# Revit family: equip-sink-clsrm-elkay-s-pacemaker-psdkrc2517-vrc
name_source: partatom
category: Plumbing Fixtures
units: mm (PartAtom-declared; Revit-internal decimal feet)

## family parameters
Always vertical = Yes
Cut with Voids When Loaded = No
OmniClass Number = 23.45.05.14.14.27
OmniClass Title = Service Sinks
Part Type = Normal
Room Calculation Point = No
Round Connector Dimension = Use Radius
Shared = No
Work Plane-Based = Yes

## types (1)
- equip-sink-clsrm-elkay-s-pacemaker-psdkrc2517-vrc
    Assembly Code = D2010410
    Back Faucet CL to Back = 0' - 2 1/4"
    Back Faucet Hole One to CL = 0' - 4"
    Back Faucet Hole OneTwo = No
    Back Faucet Hole OneTwo Top = 0' - 0 1/8"
    Back Faucet Hole Three = No
    Back Faucet Hole Three Top = 0' - 0 1/8"
    Bowl Depth = 0' - 7 1/8"
    Bowl Drain Location FB = 0' - 6 3/4"
    Bowl Length = 1' - 4"
    Bowl Width = 1' - 1 1/2"
    Bubbler Back Left = Yes
    Bubbler Back Left Top = 0' - 0 1/2"
    Bubbler Back Right = No
    Bubbler Back Right Top = 0' - 0 1/8"
    Bubbler CW Flow Rate = 2 GPM
    Bubbler Front Left = No
    Bubbler Front Left Radius = 0' - 0 9/16"
    Bubbler Front Left Top = 0' - 0 1/8"
    Bubbler Front Right = Yes
    Bubbler Front Right Radius = 0' - 0 9/16"
    Bubbler Front Right Top = 0' - 0 1/2"
    Bubbler Left From Edge = 0' - 2 1/4"
    Bubbler Material = Metal - Steel - Stainless - Chrome
    Bubbler Nominal Dia = 0' - 0 1/2"
    Bubbler Nominal Radius = 0' - 0 1/4"
    Bubbler Part = LKVR1141A
    Bubbler Right from Edge = 0' - 2 1/4"
    CW Flow Rate = 2 GPM
    Default Elevation = 3' - 0"
    Description = Lustertone Classroom Single Bowl Sink
    Drain CL LR to Left Bowl Edge = 0' - 8"
    Drain Material = Metal - Steel - Stainless - Chrome
    Drain Part = LKVR18
    Faucet Material = Metal - Steel - Stainless - Chrome
    Faucet Part = LKDCVR2085-L
    HW Flow Rate = 2 GPM
    Left Faucet Hole OneTwo = No
    Left Faucet Hole OneTwo Top = 0' - 0 1/8"
    Left Faucet Hole Three = No
    Left Faucet Hole Three Top = 0' - 0 1/8"
    Manufacturer = Elkay Manufacturing
    MasterFormat Number = 22.42.16.16
    MasterFormat Title = Commercial Sinks
    Minimum Cabinet Width = 30"
    Model = PSDKRC2517VRC
    Nominal Dia = 0' - 0 3/8"
    Nominal Radius = 0' - 0 3/16"
    OmniClass Code = 23.45.05.14.14.27
    OmniClass Title = Service Sinks
    Right Faucet Hole One to CL = 0' - 4"
    Right Faucet Hole OneTwo = No
    Right Faucet Hole OneTwo Top = 0' - 0 1/8"
    Right Faucet Hole Three = No
    Right Faucet Hole Three Top = 0' - 0 1/8"
    Sanitary Flow Rate = 10 GPM
    Sanitary Nominal Dia = 0' - 1 1/2"
    Sanitary Nominal Radius = 0' - 0 3/4"
    Sink Ledge Back Width = 0' - 1 3/4"
    Sink Ledge Back Width Hidden = 0' - 1 3/4"
    Sink Ledge Front Width = 0' - 1 3/4"
    Sink Ledge Front Width Hidden = 0' - 1 3/4"
    Sink Ledge Left Width = 0' - 4 1/2"
    Sink Ledge Left Width Hidden = 0' - 4 1/2"
    Sink Ledge Right Width = 0' - 4 1/2"
    Sink Ledge Right Width Hidden = 0' - 4 1/2"
    Sink Length = 2' - 1"
    Sink Material = Metal - Steel - Stainless - Chrome
    Sink Part = PSDKR2517-2
    Sink Width = 1' - 5"
    Specification Sheet URL = http://www.elkayusa.com
    Stem Material = Metal - Steel
    URL = www.elkayusa.com

## geometry (parser evidence)
native form markers: Sweep x12
no freeform markers — native parametric forms only
